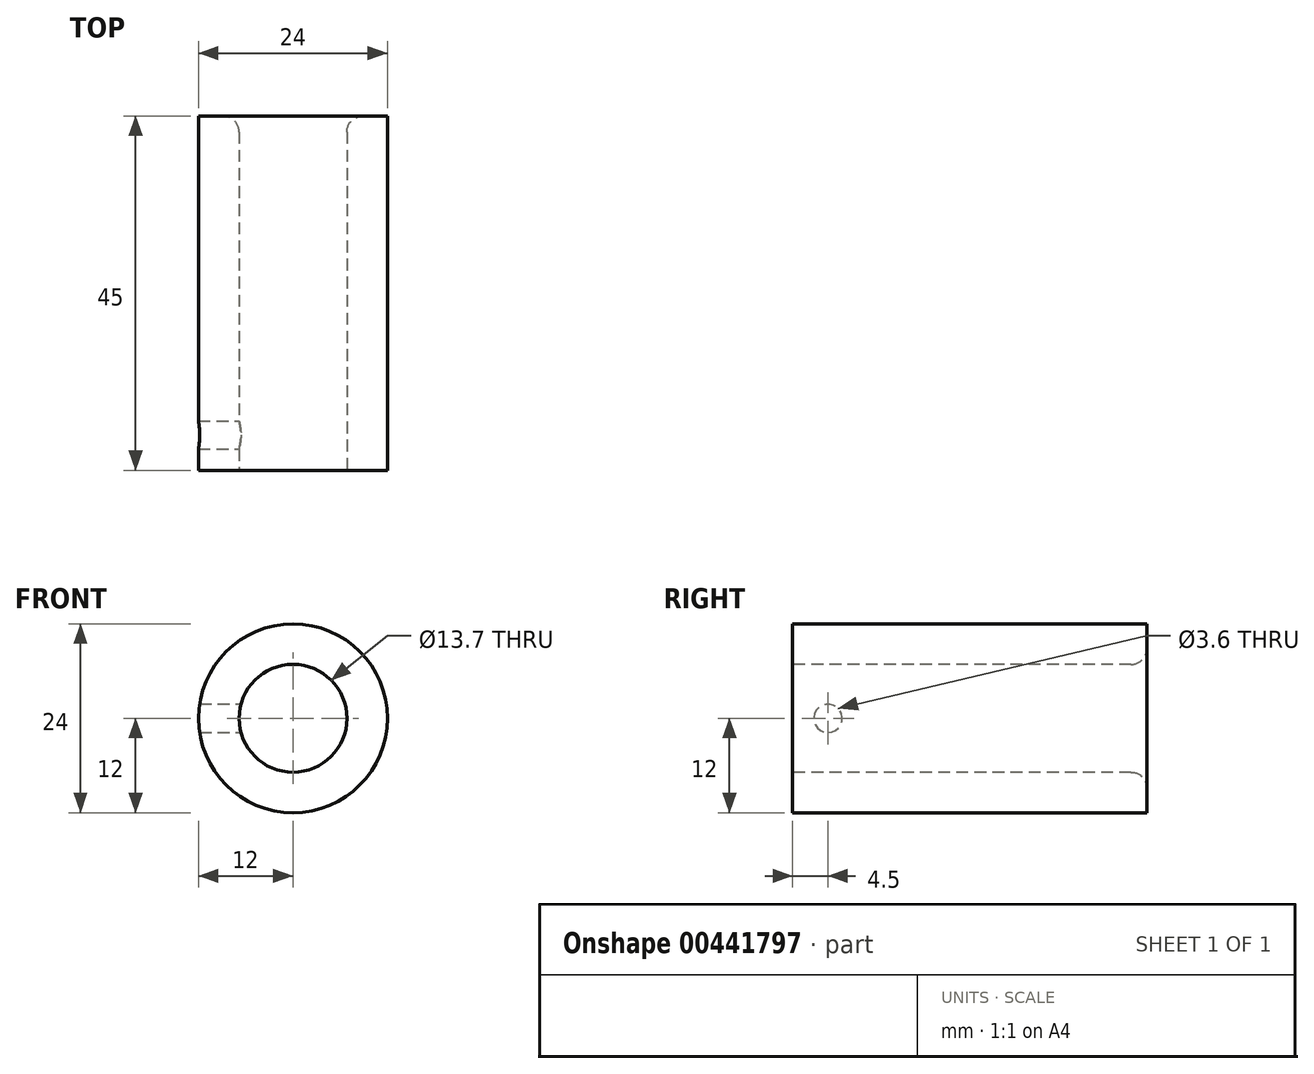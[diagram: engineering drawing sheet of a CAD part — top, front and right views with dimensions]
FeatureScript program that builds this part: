
annotation { "Feature Type Name" : "Feature", "Feature Type Description" : "" }
export const myFeature = defineFeature(function(context is Context, id is Id, definition is map)
    precondition{}
    {
        {
            var Q0;
            Q0=qCreatedBy(makeId("Front.planeOp"),FACE);
            var sketch = newSketch(context, id + "F0", { "sketchPlane" : qUnion([Q0])});
            skCircle(sketch, "E0", {"center": v(0, 0) * mm, "radius": 12 * mm});
            skSolve(sketch);
        }
        {
            var Q0;
            Q0=makeQuery(id+"F0.imprint","IMPRINT",FACE,{"disambiguationData":[TD([[makeQuery(id+"F0.imprint","IMPRINT",EDGE,{"derivedFrom":sQuery(id+"F0.wireOp",EDGE,"E0")}),1.0]])]});
            extrude(context, id + "F1", {"entities" : qUnion([Q0]), "depth" : 45 * mm});
        }
        {
            var Q0;
            Q0=makeQuery(id+"F1.opExtrude","CAP_FACE",FACE,{"disambiguationData":[OSD([sQuery(id+"F0.wireOp",EDGE,"E0")])],"isStart":false});
            var sketch = newSketch(context, id + "F2", { "sketchPlane" : qUnion([Q0])});
            skCircle(sketch, "E1", {"center": v(0, 0) * mm, "radius": 6.85 * mm});
            skSolve(sketch);
        }
        {
            var Q0;
            Q0=makeQuery(id+"F2.imprint","IMPRINT",FACE,{"disambiguationData":[TD([[makeQuery(id+"F2.imprint","IMPRINT",EDGE,{"derivedFrom":sQuery(id+"F2.wireOp",EDGE,"E1")}),1.0]])]});
            extrude(context, id + "F3", {"entities" : qUnion([Q0]), "operationType" : NewBodyOperationType.REMOVE, "oppositeDirection" : true, "depth" : 50 * mm});
        }
        {
            var Q0;
            Q0=qCreatedBy(makeId("Right.planeOp"),FACE);
            var sketch = newSketch(context, id + "F4", { "sketchPlane" : qUnion([Q0])});
            skCircle(sketch, "E2", {"center": v(-40.5, 0) * mm, "radius": 1.8 * mm});
            skSolve(sketch);
        }
        {
            var Q0;
            Q0=makeQuery(id+"F4.imprint","IMPRINT",FACE,{"disambiguationData":[TD([[makeQuery(id+"F4.imprint","IMPRINT",EDGE,{"derivedFrom":sQuery(id+"F4.wireOp",EDGE,"E2")}),1.0]])]});
            extrude(context, id + "F5", {"entities" : qUnion([Q0]), "operationType" : NewBodyOperationType.REMOVE, "oppositeDirection" : true, "depth" : 25 * mm});
        }
        {
            var Q0;
            Q0=makeQuery(id+"F3.boolean.opBoolean","INTERSECT",EDGE,{"derivedFrom":[makeQuery(id+"F1.opExtrude","CAP_FACE",FACE,{"disambiguationData":[OSD([sQuery(id+"F0.wireOp",EDGE,"E0")])],"isStart":true}),makeQuery(id+"F3.opExtrude","SWEPT_FACE",FACE,{"disambiguationData":[OSD([sQuery(id+"F2.wireOp",EDGE,"E1")])]})]});
            fillet(context, id + "F6", {"entities" : qUnion([Q0]), "radius" : 2 * mm, "tangentPropagation" : true, "allowEdgeOverflow" : false});
        }
    });
